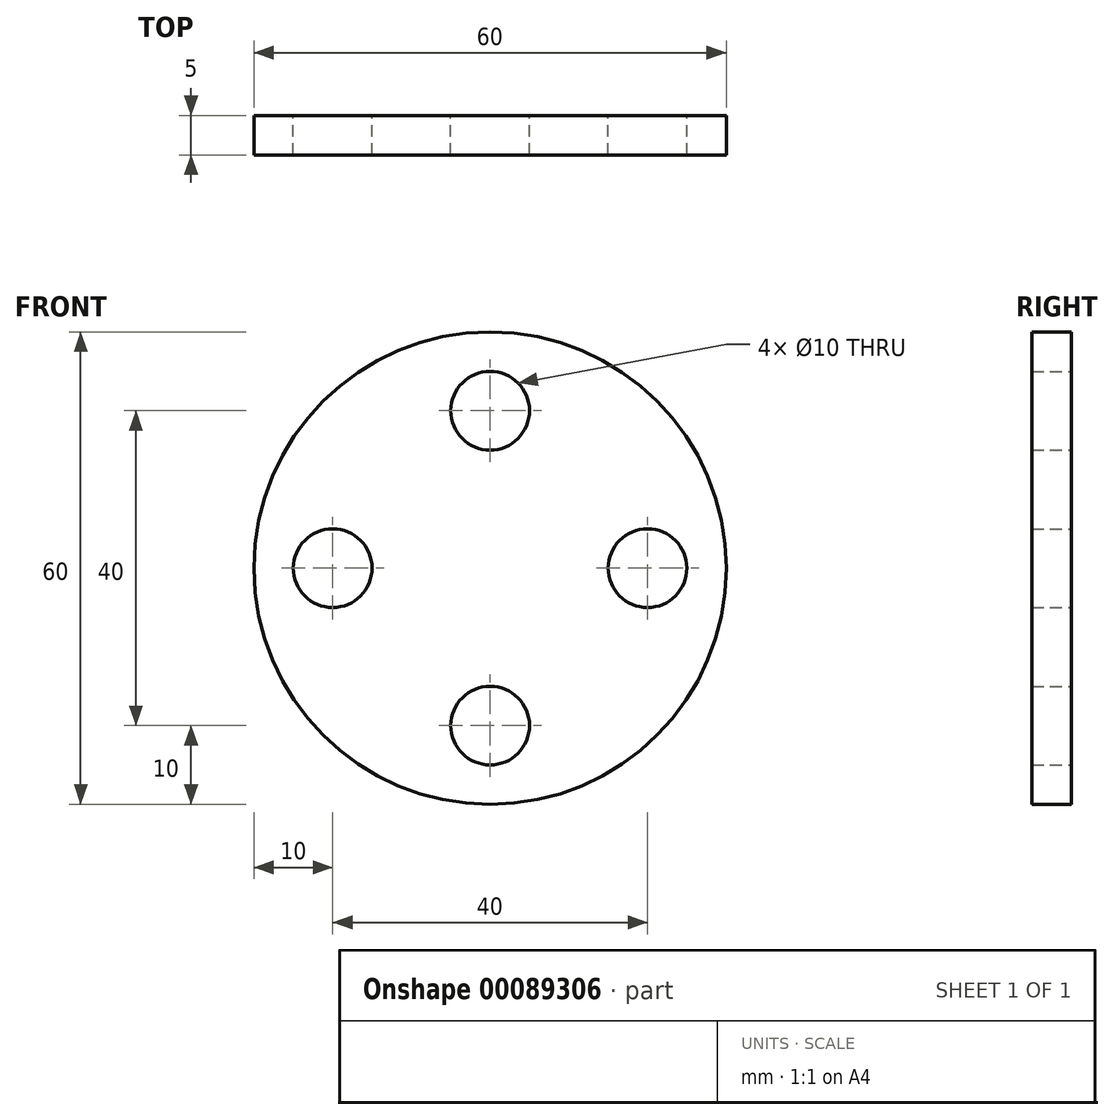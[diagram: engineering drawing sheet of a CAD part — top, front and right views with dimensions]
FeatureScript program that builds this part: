
annotation { "Feature Type Name" : "Feature", "Feature Type Description" : "" }
export const myFeature = defineFeature(function(context is Context, id is Id, definition is map)
    precondition{}
    {
        {
            var Q0;
            Q0=qCreatedBy(makeId("Front.planeOp"),FACE);
            var sketch = newSketch(context, id + "F0", { "sketchPlane" : qUnion([Q0])});
            skCircle(sketch, "E0", {"center": v(0, 0) * mm, "radius": 20 * mm, "construction": true});
            skCircle(sketch, "E1", {"center": v(0, 0) * mm, "radius": 30 * mm});
            skLineSegment(sketch, "E2", {"start": v(0, 38.07) * mm, "end": v(0, -39.23) * mm, "construction": true});
            skLineSegment(sketch, "E3", {"start": v(-43.18, 0) * mm, "end": v(49.74, 0) * mm, "construction": true});
            skCircle(sketch, "E4", {"center": v(0, 20) * mm, "radius": 5 * mm});
            skCircle(sketch, "E5", {"center": v(-20, 0) * mm, "radius": 5 * mm});
            skCircle(sketch, "E6", {"center": v(0, -20) * mm, "radius": 5 * mm});
            skCircle(sketch, "E7", {"center": v(20, 0) * mm, "radius": 5 * mm});
            skSolve(sketch);
        }
        {
            var Q0;
            Q0 = qSketchRegion(id + "F0", true);
            extrude(context, id + "F1", {"entities" : qUnion([Q0]), "depth" : 5 * mm});
        }
    });
